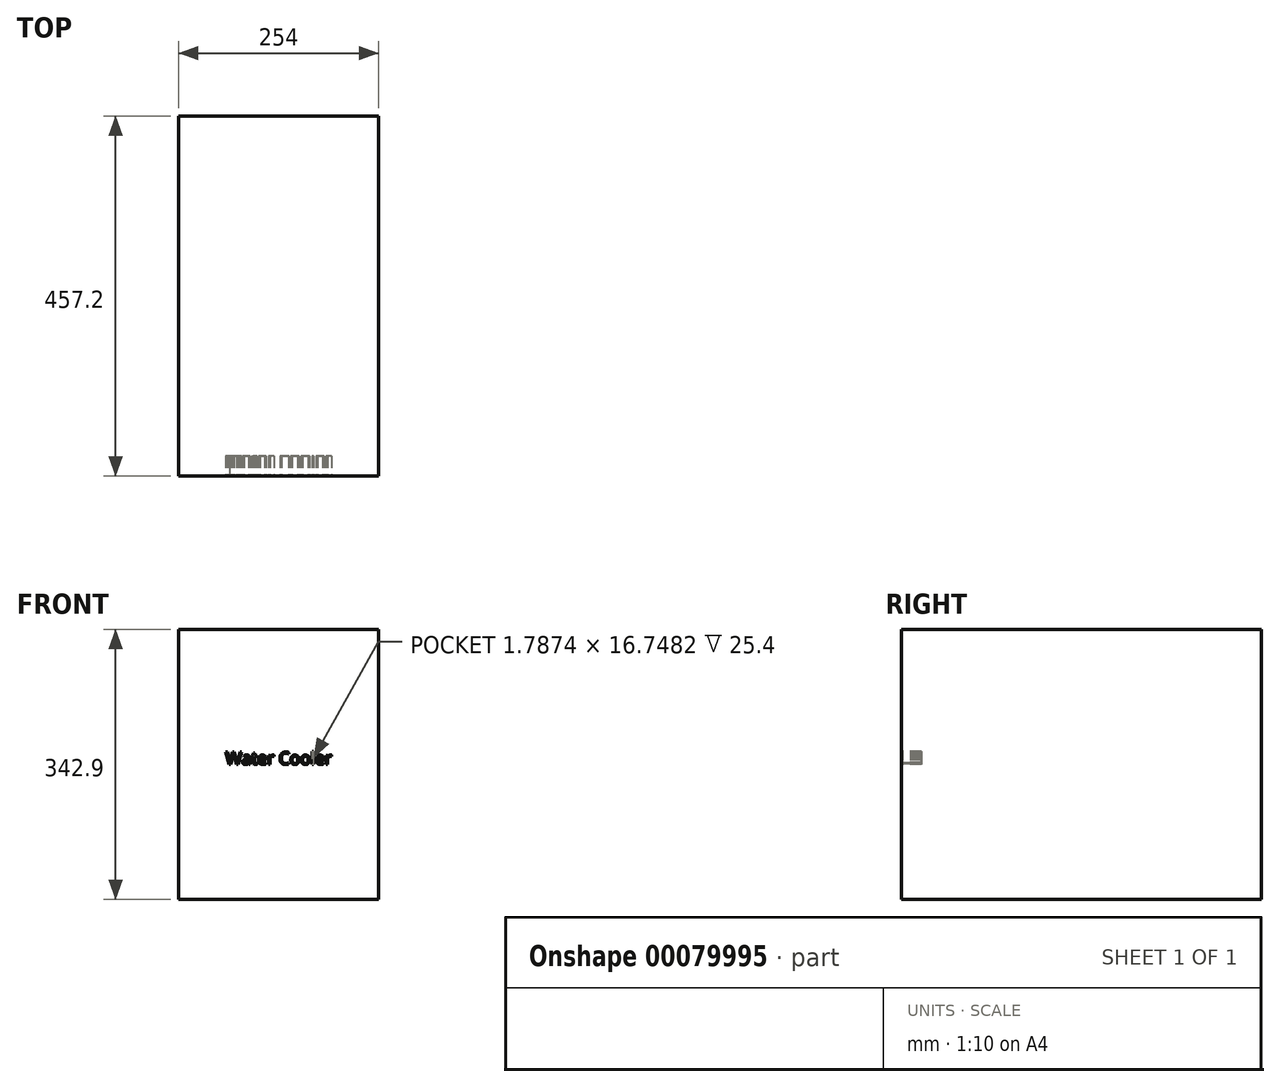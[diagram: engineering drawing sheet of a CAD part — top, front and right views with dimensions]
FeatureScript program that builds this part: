
annotation { "Feature Type Name" : "Feature", "Feature Type Description" : "" }
export const myFeature = defineFeature(function(context is Context, id is Id, definition is map)
    precondition{}
    {
        {
            var Q0;
            Q0=qCreatedBy(makeId("Front.planeOp"),FACE);
            var sketch = newSketch(context, id + "F0", { "sketchPlane" : qUnion([Q0])});
            skLineSegment(sketch, "E0.bottom", {"start": v(127, 171.45) * mm, "end": v(-127, 171.45) * mm});
            skLineSegment(sketch, "E0.top", {"start": v(127, -171.45) * mm, "end": v(-127, -171.45) * mm});
            skLineSegment(sketch, "E0.left", {"start": v(127, 171.45) * mm, "end": v(127, -171.45) * mm});
            skLineSegment(sketch, "E0.right", {"start": v(-127, 171.45) * mm, "end": v(-127, -171.45) * mm});
            skPoint(sketch, "E0.middle", {"position": v(0, 0) * mm});
            skSolve(sketch);
        }
        {
            var Q0;
            Q0=makeQuery(id+"F0.imprint","IMPRINT",FACE,{"disambiguationData":[TD([[makeQuery(id+"F0.imprint","IMPRINT",EDGE,{"derivedFrom":sQuery(id+"F0.wireOp",EDGE,"E0.bottom")}),1.0]])]});
            extrude(context, id + "F1", {"entities" : qUnion([Q0]), "oppositeDirection" : true, "depth" : 457.2 * mm});
        }
        {
            var Q0;
            Q0=makeQuery(id+"F1.opExtrude","CAP_FACE",FACE,{"disambiguationData":[OSD([sQuery(id+"F0.wireOp",EDGE,"E0.bottom"),sQuery(id+"F0.wireOp",EDGE,"E0.top"),sQuery(id+"F0.wireOp",EDGE,"E0.left"),sQuery(id+"F0.wireOp",EDGE,"E0.right")])],"isStart":true});
            var sketch = newSketch(context, id + "F2", { "sketchPlane" : qUnion([Q0])});
            skText(sketch, "E1", { "text": "Water Cooler", "fontName": "OpenSans-Regular.ttf"});
            const initialGuessF2  = {"E1": [-0.06732, 0, 1, 0, 0.01587]};
            skSetInitialGuess(sketch, initialGuessF2);
            skSolve(sketch);
        }
        {
            var Q0;
            Q0 = qSketchRegion(id + "F2", true);
            extrude(context, id + "F3", {"entities" : qUnion([Q0]), "operationType" : NewBodyOperationType.REMOVE, "oppositeDirection" : true, "depth" : 25.4 * mm});
        }
    });
